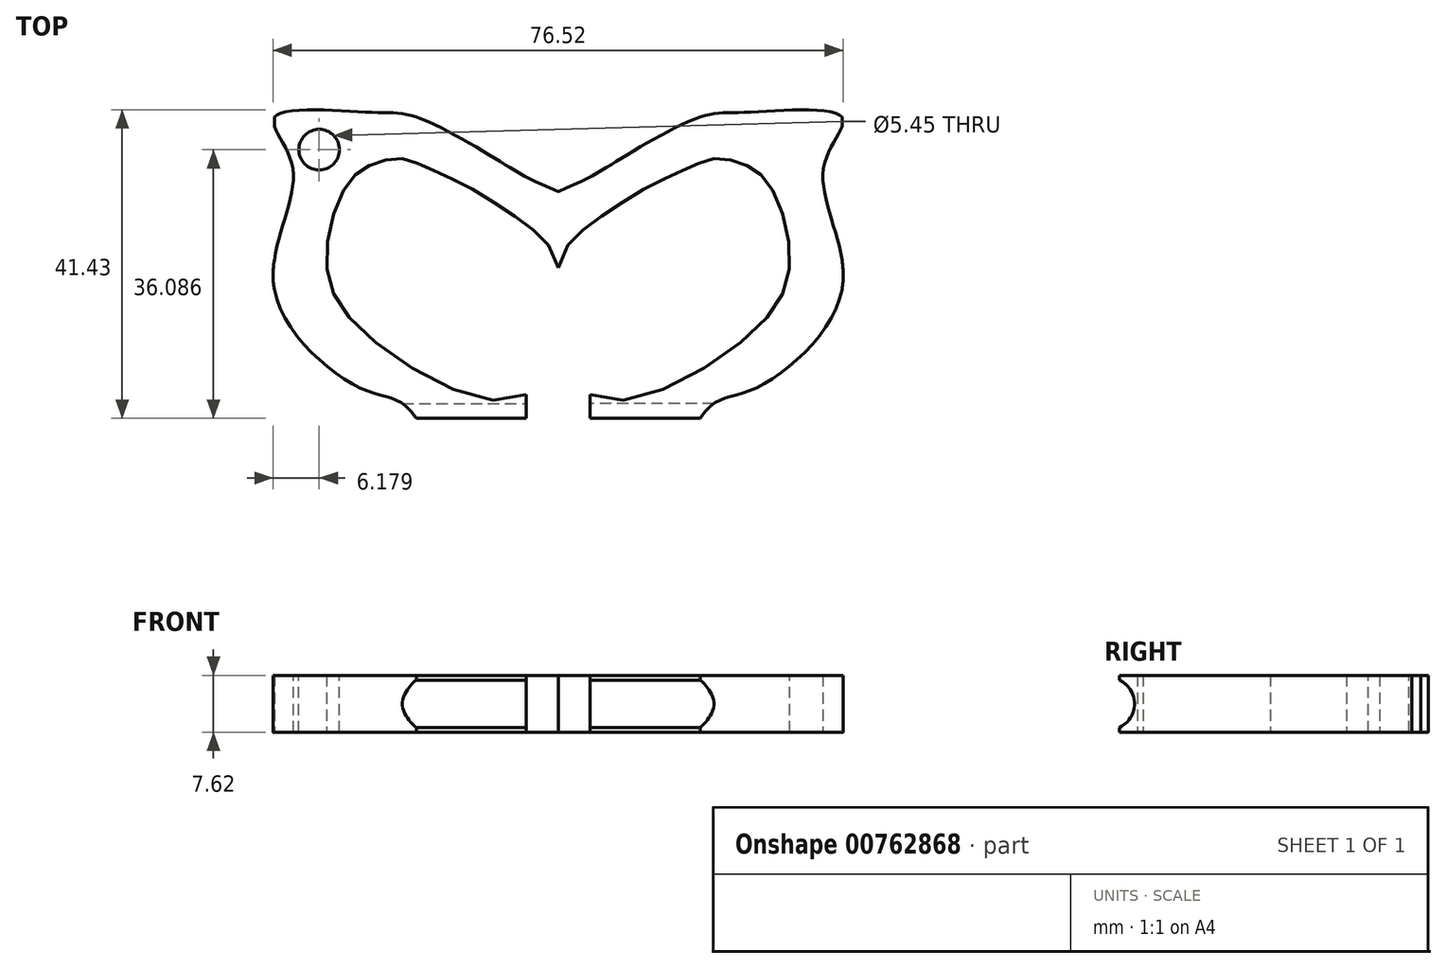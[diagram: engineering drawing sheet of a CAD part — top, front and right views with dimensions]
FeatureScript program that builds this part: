
annotation { "Feature Type Name" : "Feature", "Feature Type Description" : "" }
export const myFeature = defineFeature(function(context is Context, id is Id, definition is map)
    precondition{}
    {
        {
            var Q0;
            Q0=qCreatedBy(makeId("Top.planeOp"),FACE);
            var sketch = newSketch(context, id + "F0", { "sketchPlane" : qUnion([Q0])});
            skLineSegment(sketch, "E0.bottom", {"start": v(-38.1, 0) * mm, "end": v(0, 0) * mm});
            skLineSegment(sketch, "E0.top", {"start": v(-38.1, 40.45) * mm, "end": v(0, 40.45) * mm});
            skLineSegment(sketch, "E0.left", {"start": v(-38.1, 0) * mm, "end": v(-38.1, 50.8) * mm});
            skLineSegment(sketch, "E0.right", {"start": v(0, 0) * mm, "end": v(0, 40.45) * mm});
            skFitSpline(sketch, "E1", {"points": [v(-19.05, 0) * mm, v(-25.6, 3.66) * mm, v(-38.1, 17.31) * mm, v(-35.64, 33.66) * mm, v(-38.1, 40.45) * mm, v(-25.58, 41.12) * mm, v(-19.05, 40.45) * mm, v(-8.37, 34.85) * mm, v(0, 30.45) * mm], "startDerivative": vector(-60.45, 91.41) * mm, "endDerivative": vector(110.68, -45.92) * mm});
            skPoint(sketch, "E2.centerSnap0", {"position": v(-31.1, 21.23) * mm});
            skLineSegment(sketch, "E3.bottom", {"start": v(-4.28, 0) * mm, "end": v(0, 0) * mm});
            skLineSegment(sketch, "E3.top", {"start": v(-4.28, 3.19) * mm, "end": v(0, 3.19) * mm});
            skLineSegment(sketch, "E3.left", {"start": v(-4.28, 0) * mm, "end": v(-4.28, 3.19) * mm});
            skLineSegment(sketch, "E3.right", {"start": v(0, 0) * mm, "end": v(0, 3.19) * mm});
            skPoint(sketch, "E4.1.internal.snap0", {"position": v(-25.6, 0) * mm});
            skPoint(sketch, "E4.2.internal.snap0", {"position": v(-45.8, 21.12) * mm});
            skFitSpline(sketch, "E4", {"points": [v(-4.28, 3.19) * mm, v(-25.6, 11.16) * mm, v(-31.1, 21.12) * mm, v(-28.53, 31.06) * mm, v(-25.28, 34.02) * mm, v(-21.14, 34.9) * mm, v(-17.49, 33.66) * mm, v(-11.7, 30.86) * mm, v(-4.28, 26.03) * mm, v(0, 20.23) * mm, v(-4.28, 3.19) * mm]});
            skSolve(sketch);
        }
        {
            var Q0;
            {var subQ0=sQuery(id+"F0.wireOp",EDGE,"E1");var subQ1=sQuery(id+"F0.wireOp",EDGE,"E0.left");var subQ3=makeQuery(id+"F0.imprint","INTERSECT",VERTEX,{"disambiguationData":[OD(2.0)],"derivedFrom":[subQ1,subQ0]});Q0=makeQuery(id+"F0.imprint","IMPRINT",FACE,{"disambiguationData":[TD([[makeQuery(id+"F0.imprint","IMPRINT",EDGE,{"disambiguationData":[TD([[subQ3,-1.0]])],"derivedFrom":subQ1}),1.0]])]});}
            var Q1;
            {var subQ0=sQuery(id+"F0.wireOp",EDGE,"E1");var subQ1=sQuery(id+"F0.wireOp",EDGE,"E0.top");var subQ3=makeQuery(id+"F0.imprint","INTERSECT",VERTEX,{"derivedFrom":[subQ1,subQ0]});Q1=makeQuery(id+"F0.imprint","IMPRINT",FACE,{"disambiguationData":[TD([[makeQuery(id+"F0.imprint","IMPRINT",EDGE,{"disambiguationData":[TD([[subQ3,1.0]])],"derivedFrom":subQ1}),1.0]])]});}
            var Q2;
            {var subQ8=sQuery(id+"F0.wireOp",EDGE,"E3.left");Q2=makeQuery(id+"F0.imprint","IMPRINT",FACE,{"disambiguationData":[TD([[makeQuery(id+"F0.imprint","IMPRINT",EDGE,{"derivedFrom":subQ8}),1.0]])]});}
            var Q3;
            {var subQ0=sQuery(id+"F0.wireOp",EDGE,"E1");var subQ1=sQuery(id+"F0.wireOp",EDGE,"E0.left");var subQ2=makeQuery(id+"F0.imprint","INTERSECT",VERTEX,{"disambiguationData":[OD(0.0)],"derivedFrom":[subQ1,subQ0]});Q3=makeQuery(id+"F0.imprint","IMPRINT",FACE,{"disambiguationData":[TD([[makeQuery(id+"F0.imprint","IMPRINT",EDGE,{"disambiguationData":[TD([[subQ2,-1.0]])],"derivedFrom":subQ1}),1.0]])]});}
            extrude(context, id + "F1", {"entities" : qUnion([Q0, Q1, Q2, Q3]), "depth" : 7.62 * mm, "offsetDistance" : 25.4 * mm});
        }
        {
            var Q0;
            Q0=makeQuery(id+"F1.opExtrude","SWEPT_FACE",FACE,{"disambiguationData":[OSD([sQuery(id+"F0.wireOp",EDGE,"E3.left")])]});
            var sketch = newSketch(context, id + "F2", { "sketchPlane" : qUnion([Q0])});
            skCircle(sketch, "E5", {"center": v(-1.47, 3.8) * mm, "radius": 3.5 * mm});
            skPoint(sketch, "E5.centerSnap0", {"position": v(-0.01, 3.8) * mm});
            skSolve(sketch);
        }
        {
            var Q0;
            Q0 = qSketchRegion(id + "F2", true);
            extrude(context, id + "F3", {"entities" : qUnion([Q0]), "operationType" : NewBodyOperationType.REMOVE, "endBound" : BoundingType.THROUGH_ALL, "oppositeDirection" : true, "depth" : 25.4 * mm, "offsetDistance" : 25.4 * mm});
        }
        {
            var Q0;
            Q0=makeQuery(id+"F1.opExtrude","SWEPT_BODY",BODY,{"disambiguationData":[OSD([sQuery(id+"F0.wireOp",EDGE,"E0.bottom"),sQuery(id+"F0.wireOp",EDGE,"E0.left"),sQuery(id+"F0.wireOp",EDGE,"E0.right"),sQuery(id+"F0.wireOp",EDGE,"E1"),sQuery(id+"F0.wireOp",EDGE,"VIvpU9DL-0KRQ-vhnE-llWS-HSkTrEKxQjya"),sQuery(id+"F0.wireOp",EDGE,"E2"),sQuery(id+"F0.wireOp",EDGE,"2ZIxEUnY-bV2S-Xhbg-eiZA-P4F7n0opV9h2"),sQuery(id+"F0.wireOp",EDGE,"XJpmClHl-YvgJ-KgLu-pxm0-jQcJAtJRcp7z"),sQuery(id+"F0.wireOp",EDGE,"aeRQv1he-otvV-J90Z-teIl-opaKG3LdSsG4"),sQuery(id+"F0.wireOp",EDGE,"E3.top"),sQuery(id+"F0.wireOp",EDGE,"E3.left")])]});
            var Q1;
            Q1=qCreatedBy(makeId("Right.planeOp"),FACE);
            mirror(context, id + "F4", {"operationType" : NewBodyOperationType.ADD, "entities" : qUnion([Q0]), "mirrorPlane" : qUnion([Q1])});
        }
        {
            var Q0;
            {var subQ0=makeQuery(id+"F1.opExtrude","CAP_FACE",FACE,{"disambiguationData":[OSD([sQuery(id+"F0.wireOp",EDGE,"E0.bottom"),sQuery(id+"F0.wireOp",EDGE,"E0.right"),sQuery(id+"F0.wireOp",EDGE,"E1"),sQuery(id+"F0.wireOp",EDGE,"E3.left"),sQuery(id+"F0.wireOp",EDGE,"E4")])],"isStart":false});Q0=makeQuery(id+"F4.boolean.opBoolean","MERGE",FACE,{"derivedFrom":[subQ0,makeQuery(id+"F4.opPattern","COPY",FACE,{"derivedFrom":subQ0,"instanceName":"1"})]});}
            var sketch = newSketch(context, id + "F5", { "sketchPlane" : qUnion([Q0])});
            skCircle(sketch, "E6", {"center": v(-32.08, 36.09) * mm, "radius": 2.73 * mm});
            skSolve(sketch);
        }
        {
            var Q0;
            Q0=makeQuery(id+"F5.imprint","IMPRINT",FACE,{"disambiguationData":[TD([[makeQuery(id+"F5.imprint","IMPRINT",EDGE,{"derivedFrom":sQuery(id+"F5.wireOp",EDGE,"E6")}),1.0]])]});
            extrude(context, id + "F6", {"entities" : qUnion([Q0]), "operationType" : NewBodyOperationType.REMOVE, "endBound" : BoundingType.THROUGH_ALL, "oppositeDirection" : true, "depth" : 25.4 * mm, "offsetDistance" : 25.4 * mm});
        }
    });
